# Revit family: 303_R16_
name_source: partatom
category: Pipe Accessories
revit_build: Autodesk Revit 2018 (Build: 20170223_1515(x64)
units: mm (PartAtom-declared; Revit-internal decimal feet)

## family parameters
Always vertical = Yes
Cut with Voids When Loaded = No
Part Type = Valve - Breaks Into
Round Connector Dimension = Use Diameter
Shared = No
Work Plane-Based = No

## types (3) — shared parameters
CAT0 = Yes
Description = Angle lockshield valve for heat systems
H4 = 2 mm  [stored 0.00656168 ft]
J2 = 2 mm  [stored 0.00656168 ft]
L1 = 9 mm  [stored 0.0295276 ft]
L2D_Min = 3048 mm  [stored 10 ft]
L3 = 9 mm  [stored 0.0295276 ft]
L4 = 9 mm  [stored 0.0295276 ft]
Manufacturer = Giacomini
QmdConnectorList = 301;D;302;D1
URL = http://www.giacomini.com
X5 = 5 mm  [stored 0.0164042 ft]
X5__ve = -5 mm  [stored -0.0164042 ft]
magiPartTypeId = 303
magiProductFamilyId = R16*
zero-valued in all types: MC_Default_elevation

## per-type parameters (varying)
- R16X032: B1=7 mm  [stored 0.0229659 ft]; B4=9 mm  [stored 0.0295276 ft]; CenSd_K1_6=9 mm  [stored 0.0295276 ft]; CenSd_W2_6=12 mm  [stored 0.0393701 ft]; CenSd_Y1_6=8 mm  [stored 0.0262467 ft]; D=10 mm; D1=10 mm; G1=8 mm  [stored 0.0262467 ft]; H3=4 mm  [stored 0.0131234 ft]; H3__ve=-4 mm  [stored -0.0131234 ft]; J=18 mm  [stored 0.0590551 ft]; J1=5 mm  [stored 0.0164042 ft]; J3=10 mm  [stored 0.0328084 ft]; K1=11 mm  [stored 0.0360892 ft]; KCAT=No; KH=7 mm  [stored 0.0229659 ft]; KH__ve=-7 mm; L=38 mm  [stored 0.124672 ft]; L2=49 mm; L2D=38 mm  [stored 0.124672 ft]; M3=12 mm  [stored 0.0393701 ft]; M3__ve=-12 mm; R1=8 mm  [stored 0.0262467 ft]; SWC=1 mm  [stored 0.00328084 ft]; W1=11 mm  [stored 0.0360892 ft]; W2=14 mm  [stored 0.0459318 ft]; W2D=10 mm  [stored 0.0328084 ft]; X1=12 mm  [stored 0.0393701 ft]; X4=5 mm  [stored 0.0164042 ft]; Y1=10 mm  [stored 0.0328084 ft]
- R16X033: B1=8 mm  [stored 0.0262467 ft]; B4=11 mm  [stored 0.0360892 ft]; CenSd_K1_6=11 mm  [stored 0.0360892 ft]; CenSd_W2_6=13 mm; CenSd_Y1_6=10 mm  [stored 0.0328084 ft]; D=15 mm; D1=15 mm; G1=10 mm  [stored 0.0328084 ft]; H3=5 mm  [stored 0.0164042 ft]; H3__ve=-5 mm  [stored -0.0164042 ft]; J=21 mm  [stored 0.0688976 ft]; J1=6 mm  [stored 0.019685 ft]; J3=12 mm  [stored 0.0393701 ft]; K1=13 mm; KCAT=No; KH=8 mm  [stored 0.0262467 ft]; KH__ve=-8 mm  [stored -0.0262467 ft]; L=40 mm; L2=51 mm; L2D=40 mm; M3=13 mm; M3__ve=-13 mm; R1=11 mm  [stored 0.0360892 ft]; SWC=1 mm  [stored 0.00328084 ft]; W1=13 mm; W2=15 mm  [stored 0.0492126 ft]; W2D=15 mm  [stored 0.0492126 ft]; X1=13 mm; X4=6 mm  [stored 0.019685 ft]; Y1=11 mm  [stored 0.0360892 ft]
- R16EX037: B1=8 mm  [stored 0.0262467 ft]; B4=11 mm  [stored 0.0360892 ft]; CenSd_K1_6=11 mm  [stored 0.0360892 ft]; CenSd_W2_6=13 mm; CenSd_Y1_6=10 mm  [stored 0.0328084 ft]; D=20 mm; D1=15 mm; G1=10 mm  [stored 0.0328084 ft]; H3=5 mm  [stored 0.0164042 ft]; H3__ve=-5 mm  [stored -0.0164042 ft]; J=21 mm  [stored 0.0688976 ft]; J1=6 mm  [stored 0.019685 ft]; J3=12 mm  [stored 0.0393701 ft]; K1=13 mm; KCAT=Yes; KH=8 mm  [stored 0.0262467 ft]; KH__ve=-8 mm  [stored -0.0262467 ft]; L=40 mm; L2=51 mm; L2D=40 mm; M3=13 mm; M3__ve=-13 mm; R1=11 mm  [stored 0.0360892 ft]; SWC=0 mm  [stored 0 ft]; W1=13 mm; W2=15 mm  [stored 0.0492126 ft]; W2D=15 mm  [stored 0.0492126 ft]; X1=13 mm; X4=6 mm  [stored 0.019685 ft]; Y1=11 mm  [stored 0.0360892 ft]

note: column(s) folded — value = type name in every type: magiProductCode, magiProductId

note: [stored X ft] marks values corroborated as IEEE doubles in the binary element streams (Revit-internal decimal feet)

## geometry (parser evidence)
native form markers: Sweep x1
no freeform markers — native parametric forms only
